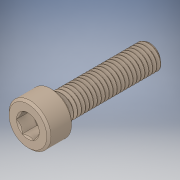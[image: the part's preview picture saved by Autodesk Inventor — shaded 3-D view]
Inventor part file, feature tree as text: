
AUTODESK INVENTOR PART (.ipt)
format: ipt  version: 2019 (Build 230136000, 136)  size: 564,736 bytes
history: mixed  units: mm
features: chamfer x1, imported_body x1
ambient origin geometry x8: Origin, YZ Plane, XZ Plane, XY Plane, X Axis, Y Axis, Z Axis, Center Point
bodies: Solid1 (imported_parasolid)
feature tree (2):
  chamfer  "Chamfer1"  [1 undecoded]
  imported_body  NMx_Import_Brep_tag  [imported B-rep: ~3 faces, bbox_mm=None]
note: 1 required parameter value undecoded (feature->parameter linkage not recoverable at this tier; creation-order binding heuristic only, values carry confidence <= 0.55)
